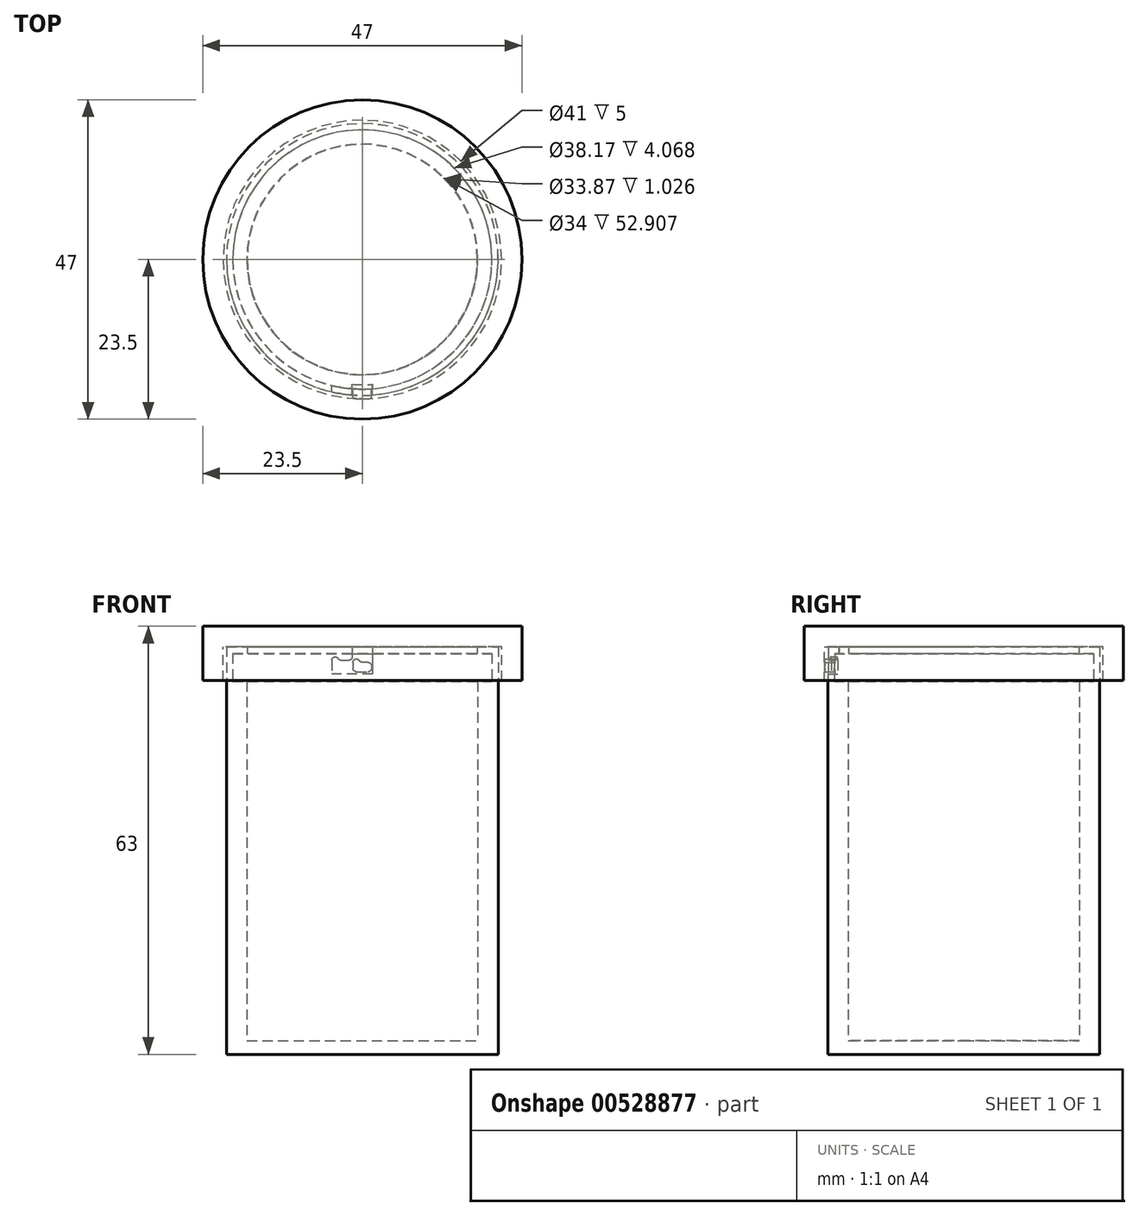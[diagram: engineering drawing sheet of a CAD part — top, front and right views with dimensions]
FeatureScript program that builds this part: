
annotation { "Feature Type Name" : "Feature", "Feature Type Description" : "" }
export const myFeature = defineFeature(function(context is Context, id is Id, definition is map)
    precondition{}
    {
        {
            var Q0;
            Q0=qCreatedBy(makeId("Front.planeOp"),FACE);
            var sketch = newSketch(context, id + "F0", { "sketchPlane" : qUnion([Q0])});
            skLineSegment(sketch, "E0", {"start": v(20, -31) * mm, "end": v(20, 29) * mm});
            skLineSegment(sketch, "E1", {"start": v(20, 29) * mm, "end": v(17, 29) * mm});
            skLineSegment(sketch, "E2", {"start": v(20, -31) * mm, "end": v(0, -31) * mm});
            skLineSegment(sketch, "E3", {"start": v(0, -31) * mm, "end": v(0, -29) * mm});
            skLineSegment(sketch, "E4", {"start": v(0, -29) * mm, "end": v(17, -29) * mm});
            skLineSegment(sketch, "E5", {"start": v(17, -29) * mm, "end": v(17, 29) * mm});
            skLineSegment(sketch, "E6", {"start": v(0, 0) * mm, "end": v(17, 0) * mm, "construction": true});
            skSolve(sketch);
        }
        {
            var Q0;
            Q0 = qSketchRegion(id + "F0", true);
            var Q1;
            Q1=sQuery(id+"F0.wireOp",EDGE,"E3");
            revolve(context, id + "F1", {"surfaceOperationType" : NewSurfaceOperationType.NEW, "entities" : qUnion([Q0]), "axis" : qUnion([Q1]), "revolveType" : RevolveType.FULL});
        }
        {
            var Q0;
            Q0=qCreatedBy(makeId("Front.planeOp"),FACE);
            var sketch = newSketch(context, id + "F2", { "sketchPlane" : qUnion([Q0])});
            skLineSegment(sketch, "E7", {"start": v(-1.5, 29) * mm, "end": v(1.5, 29) * mm});
            skLineSegment(sketch, "E8", {"start": v(1.5, 29) * mm, "end": v(1.5, 25) * mm});
            skLineSegment(sketch, "E9", {"start": v(1.5, 25) * mm, "end": v(-4.5, 25) * mm});
            skLineSegment(sketch, "E10", {"start": v(-4.5, 25) * mm, "end": v(-4.5, 27) * mm});
            skLineSegment(sketch, "E11", {"start": v(-3.13, 27) * mm, "end": v(-2, 27) * mm});
            skLineSegment(sketch, "E12", {"start": v(-1.5, 27.5) * mm, "end": v(-1.5, 29) * mm});
            skArc(sketch, "E13", {"start": v(-3.57, 27.25) * mm, "mid": v(-4.13, 27.48) * mm, "end": v(-4.5, 27) * mm});
            skArc(sketch, "E14", {"start": v(-3.57, 27.25) * mm, "mid": v(-3.38, 27.07) * mm, "end": v(-3.13, 27) * mm});
            skArc(sketch, "E15", {"start": v(-2, 27) * mm, "mid": v(-1.65, 27.15) * mm, "end": v(-1.5, 27.5) * mm});
            skPoint(sketch, "E16", {"position": v(0, 29) * mm});
            skSolve(sketch);
        }
        {
            var Q0;
            Q0 = qSketchRegion(id + "F2", true);
            extrude(context, id + "F3", {"entities" : qUnion([Q0]), "operationType" : NewBodyOperationType.REMOVE, "depth" : 25 * mm, "offsetDistance" : 25 * mm});
        }
        {
            var Q0;
            Q0=qCreatedBy(makeId("Right.planeOp"),FACE);
            var sketch = newSketch(context, id + "F4", { "sketchPlane" : qUnion([Q0])});
            skLineSegment(sketch, "E17.bottom", {"start": v(-18.43, 29) * mm, "end": v(-16.93, 29) * mm});
            skLineSegment(sketch, "E17.top", {"start": v(-18.43, 25) * mm, "end": v(-16.93, 25) * mm});
            skLineSegment(sketch, "E17.left", {"start": v(-18.43, 29) * mm, "end": v(-18.43, 25) * mm});
            skLineSegment(sketch, "E17.right", {"start": v(-16.93, 29) * mm, "end": v(-16.93, 25) * mm});
            skSolve(sketch);
        }
        {
            var Q0;
            Q0 = qSketchRegion(id + "F4", true);
            var Q1;
            Q1=sQuery(id+"F0.wireOp",EDGE,"E3");
            revolve(context, id + "F5", {"operationType" : NewBodyOperationType.ADD, "surfaceOperationType" : NewSurfaceOperationType.NEW, "entities" : qUnion([Q0]), "axis" : qUnion([Q1]), "revolveType" : RevolveType.FULL});
        }
        {
            var Q0;
            Q0=qCreatedBy(makeId("Front.planeOp"),FACE);
            var sketch = newSketch(context, id + "F6", { "sketchPlane" : qUnion([Q0])});
            skLineSegment(sketch, "E18", {"start": v(0, 29) * mm, "end": v(20.5, 29) * mm});
            skLineSegment(sketch, "E19", {"start": v(20.5, 29) * mm, "end": v(20.5, 24) * mm});
            skLineSegment(sketch, "E20", {"start": v(20.5, 24) * mm, "end": v(23.5, 24) * mm});
            skLineSegment(sketch, "E21", {"start": v(23.5, 24) * mm, "end": v(23.5, 32) * mm});
            skLineSegment(sketch, "E22", {"start": v(23.5, 32) * mm, "end": v(0, 32) * mm});
            skLineSegment(sketch, "E23", {"start": v(0, 32) * mm, "end": v(0, 29) * mm});
            skSolve(sketch);
        }
        {
            var Q0;
            Q0 = qSketchRegion(id + "F6", true);
            var Q1;
            Q1=sQuery(id+"F6.wireOp",EDGE,"E23");
            revolve(context, id + "F7", {"surfaceOperationType" : NewSurfaceOperationType.NEW, "entities" : qUnion([Q0]), "axis" : qUnion([Q1]), "revolveType" : RevolveType.FULL});
        }
        {
            var Q0;
            Q0=qCreatedBy(makeId("Front.planeOp"),FACE);
            var sketch = newSketch(context, id + "F8", { "sketchPlane" : qUnion([Q0])});
            skArc(sketch, "E24", {"start": v(-0.43, 26.95) * mm, "mid": v(-1, 27.18) * mm, "end": v(-1.37, 26.7) * mm});
            skLineSegment(sketch, "E25", {"start": v(-1.37, 26.7) * mm, "end": v(-1.37, 25.8) * mm});
            skLineSegment(sketch, "E26", {"start": v(-0.87, 25.3) * mm, "end": v(0.83, 25.3) * mm});
            skLineSegment(sketch, "E27", {"start": v(1.33, 25.8) * mm, "end": v(1.33, 26.2) * mm});
            skLineSegment(sketch, "E28", {"start": v(0.83, 26.7) * mm, "end": v(0, 26.7) * mm});
            skArc(sketch, "E29", {"start": v(-0.43, 26.95) * mm, "mid": v(-0.25, 26.77) * mm, "end": v(0, 26.7) * mm});
            skArc(sketch, "E30", {"start": v(1.33, 26.2) * mm, "mid": v(1.19, 26.55) * mm, "end": v(0.83, 26.7) * mm});
            skArc(sketch, "E31", {"start": v(0.83, 25.3) * mm, "mid": v(1.19, 25.45) * mm, "end": v(1.33, 25.8) * mm});
            skArc(sketch, "E32", {"start": v(-1.37, 25.8) * mm, "mid": v(-1.22, 25.45) * mm, "end": v(-0.87, 25.3) * mm});
            skSolve(sketch);
        }
        {
            var Q0;
            Q0 = qSketchRegion(id + "F8", true);
            extrude(context, id + "F9", {"entities" : qUnion([Q0]), "operationType" : NewBodyOperationType.ADD, "depth" : 22 * mm, "offsetDistance" : 25 * mm});
        }
        {
            var Q0;
            Q0=qCreatedBy(makeId("Right.planeOp"),FACE);
            var sketch = newSketch(context, id + "F10", { "sketchPlane" : qUnion([Q0])});
            skLineSegment(sketch, "E33.bottom", {"start": v(-19.08, 23.9) * mm, "end": v(0, 23.9) * mm});
            skLineSegment(sketch, "E33.top", {"start": v(-19.08, 27.97) * mm, "end": v(0, 27.97) * mm});
            skLineSegment(sketch, "E33.left", {"start": v(-19.08, 27.97) * mm, "end": v(-19.08, 23.9) * mm});
            skLineSegment(sketch, "E33.right", {"start": v(0, 27.97) * mm, "end": v(0, 23.9) * mm});
            skSolve(sketch);
        }
        {
            var Q0;
            Q0 = qSketchRegion(id + "F10", true);
            var Q1;
            Q1=sQuery(id+"F10.wireOp",EDGE,"E33.right");
            revolve(context, id + "F11", {"operationType" : NewBodyOperationType.REMOVE, "surfaceOperationType" : NewSurfaceOperationType.NEW, "entities" : qUnion([Q0]), "axis" : qUnion([Q1]), "revolveType" : RevolveType.FULL, "oppositeDirection" : true});
        }
    });
